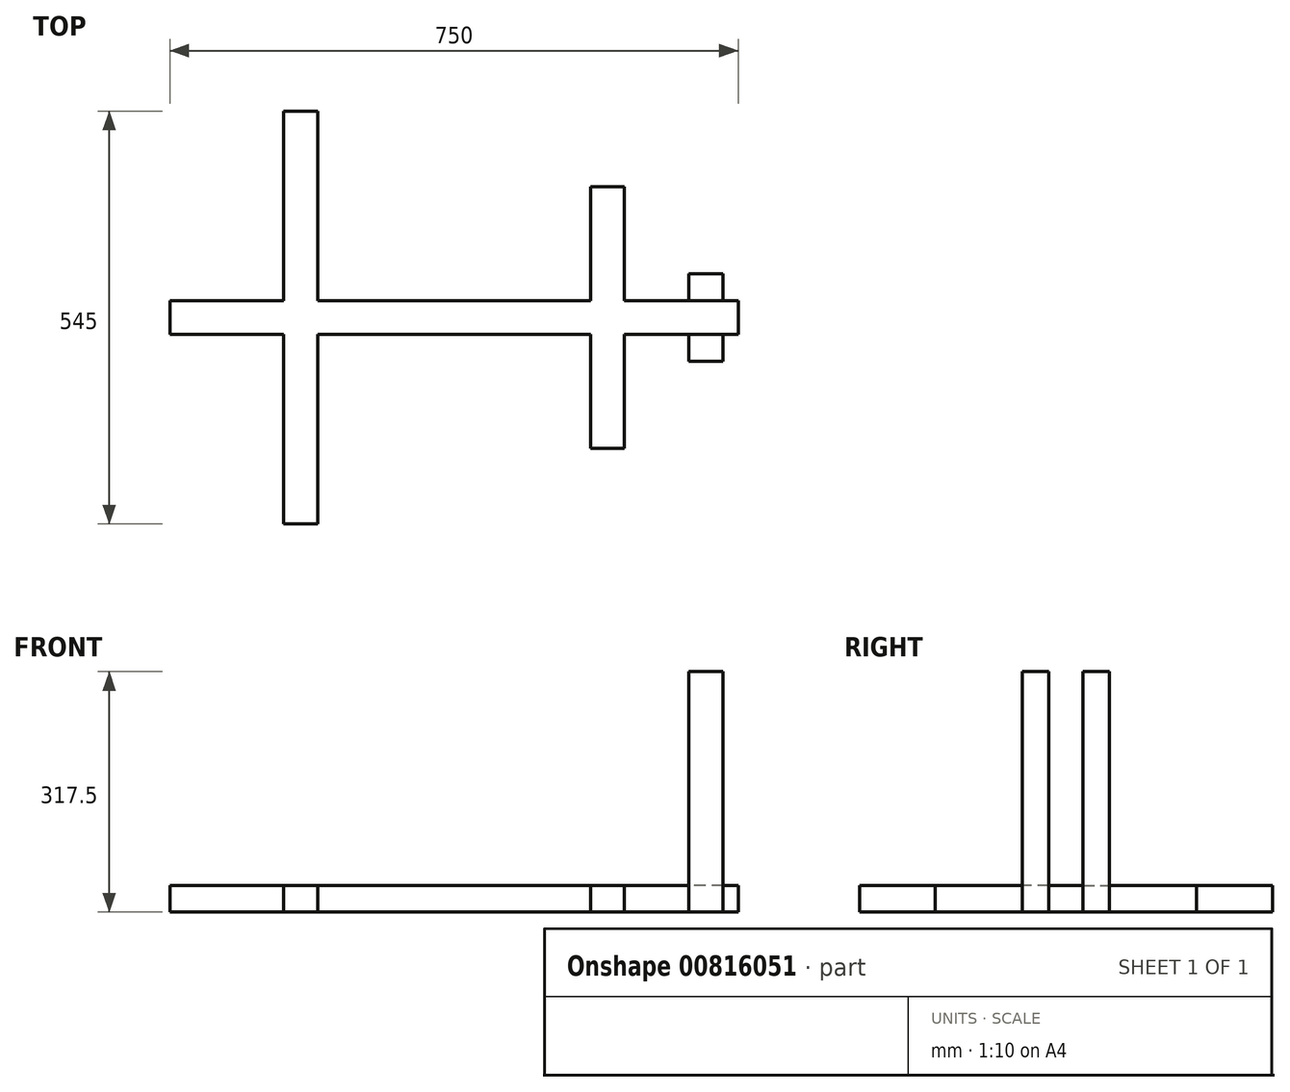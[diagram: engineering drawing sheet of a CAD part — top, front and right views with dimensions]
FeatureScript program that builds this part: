
annotation { "Feature Type Name" : "Feature", "Feature Type Description" : "" }
export const myFeature = defineFeature(function(context is Context, id is Id, definition is map)
    precondition{}
    {
        {
            var Q0;
            Q0=qCreatedBy(makeId("Front.planeOp"),FACE);
            var sketch = newSketch(context, id + "F0", { "sketchPlane" : qUnion([Q0])});
            skLineSegment(sketch, "E0.bottom", {"start": v(375, 17.5) * mm, "end": v(-375, 17.5) * mm});
            skLineSegment(sketch, "E0.top", {"start": v(375, -17.5) * mm, "end": v(-375, -17.5) * mm});
            skLineSegment(sketch, "E0.left", {"start": v(375, 17.5) * mm, "end": v(375, -17.5) * mm});
            skLineSegment(sketch, "E0.right", {"start": v(-375, 17.5) * mm, "end": v(-375, -17.5) * mm});
            skPoint(sketch, "E0.middle", {"position": v(0, 0) * mm});
            skSolve(sketch);
        }
        {
            var Q0;
            Q0=makeQuery(id+"F0.imprint","IMPRINT",FACE,{"disambiguationData":[TD([[makeQuery(id+"F0.imprint","IMPRINT",EDGE,{"derivedFrom":sQuery(id+"F0.wireOp",EDGE,"E0.bottom")}),1.0]])]});
            extrude(context, id + "F1", {"entities" : qUnion([Q0]), "endBound" : BoundingType.SYMMETRIC, "depth" : 45 * mm, "offsetDistance" : 25 * mm, "hasSecondDirection" : true, "secondDirectionOppositeDirection" : true, "secondDirectionDepth" : 25 * mm});
        }
        {
            var Q0;
            Q0=qCreatedBy(makeId("Top.planeOp"),FACE);
            var sketch = newSketch(context, id + "F2", { "sketchPlane" : qUnion([Q0])});
            skLineSegment(sketch, "E1.bottom", {"start": v(-180, 22.5) * mm, "end": v(-225, 22.5) * mm});
            skLineSegment(sketch, "E1.top", {"start": v(-180, 272.5) * mm, "end": v(-225, 272.5) * mm});
            skLineSegment(sketch, "E1.left", {"start": v(-180, 22.5) * mm, "end": v(-180, 272.5) * mm});
            skLineSegment(sketch, "E1.right", {"start": v(-225, 22.5) * mm, "end": v(-225, 272.5) * mm});
            skLineSegment(sketch, "E2", {"start": v(-277.97, 0) * mm, "end": v(292.1, 0) * mm, "construction": true});
            skLineSegment(sketch, "E3.MirrorCS", {"start": v(-225, -22.5) * mm, "end": v(-225, -272.5) * mm});
            skLineSegment(sketch, "E4.MirrorCS", {"start": v(-180, -22.5) * mm, "end": v(-180, -272.5) * mm});
            skLineSegment(sketch, "E5.MirrorCS", {"start": v(-180, -272.5) * mm, "end": v(-225, -272.5) * mm});
            skLineSegment(sketch, "E6.MirrorCS", {"start": v(-180, -22.5) * mm, "end": v(-225, -22.5) * mm});
            skLineSegment(sketch, "E7.bottom", {"start": v(180, 22.5) * mm, "end": v(225, 22.5) * mm});
            skLineSegment(sketch, "E7.top", {"start": v(180, 172.5) * mm, "end": v(225, 172.5) * mm});
            skLineSegment(sketch, "E7.left", {"start": v(180, 22.5) * mm, "end": v(180, 172.5) * mm});
            skLineSegment(sketch, "E7.right", {"start": v(225, 22.5) * mm, "end": v(225, 172.5) * mm});
            skLineSegment(sketch, "E8.MirrorCS", {"start": v(225, -22.5) * mm, "end": v(225, -172.5) * mm});
            skLineSegment(sketch, "E9.MirrorCS", {"start": v(180, -172.5) * mm, "end": v(225, -172.5) * mm});
            skLineSegment(sketch, "E10.MirrorCS", {"start": v(180, -22.5) * mm, "end": v(180, -172.5) * mm});
            skLineSegment(sketch, "E11.MirrorCS", {"start": v(180, -22.5) * mm, "end": v(225, -22.5) * mm});
            skSolve(sketch);
        }
        {
            var Q0;
            Q0=makeQuery(id+"F2.imprint","IMPRINT",FACE,{"disambiguationData":[TD([[makeQuery(id+"F2.imprint","IMPRINT",EDGE,{"derivedFrom":sQuery(id+"F2.wireOp",EDGE,"E7.bottom")}),1.0]])]});
            var Q1;
            Q1=makeQuery(id+"F2.imprint","IMPRINT",FACE,{"disambiguationData":[TD([[makeQuery(id+"F2.imprint","IMPRINT",EDGE,{"derivedFrom":sQuery(id+"F2.wireOp",EDGE,"E8.MirrorCS")}),-1.0]])]});
            var Q2;
            Q2=makeQuery(id+"F2.imprint","IMPRINT",FACE,{"disambiguationData":[TD([[makeQuery(id+"F2.imprint","IMPRINT",EDGE,{"derivedFrom":sQuery(id+"F2.wireOp",EDGE,"E1.bottom")}),-1.0]])]});
            var Q3;
            Q3=makeQuery(id+"F2.imprint","IMPRINT",FACE,{"disambiguationData":[TD([[makeQuery(id+"F2.imprint","IMPRINT",EDGE,{"derivedFrom":sQuery(id+"F2.wireOp",EDGE,"E3.MirrorCS")}),1.0]])]});
            extrude(context, id + "F3", {"entities" : qUnion([Q0, Q1, Q2, Q3]), "operationType" : NewBodyOperationType.ADD, "endBound" : BoundingType.SYMMETRIC, "depth" : 35 * mm, "offsetDistance" : 25 * mm});
        }
        {
            var Q0;
            Q0=qCreatedBy(makeId("Top.planeOp"),FACE);
            var sketch = newSketch(context, id + "F4", { "sketchPlane" : qUnion([Q0])});
            skLineSegment(sketch, "E12.bottom", {"start": v(310, 22.5) * mm, "end": v(355, 22.5) * mm});
            skLineSegment(sketch, "E12.top", {"start": v(310, 57.5) * mm, "end": v(355, 57.5) * mm});
            skLineSegment(sketch, "E12.left", {"start": v(310, 22.5) * mm, "end": v(310, 57.5) * mm});
            skLineSegment(sketch, "E12.right", {"start": v(355, 22.5) * mm, "end": v(355, 57.5) * mm});
            skLineSegment(sketch, "E13", {"start": v(416.08, 0) * mm, "end": v(-404.27, 0) * mm, "construction": true});
            skLineSegment(sketch, "E14.MirrorCS", {"start": v(310, -57.5) * mm, "end": v(355, -57.5) * mm});
            skLineSegment(sketch, "E15.MirrorCS", {"start": v(355, -22.5) * mm, "end": v(355, -57.5) * mm});
            skLineSegment(sketch, "E16.MirrorCS", {"start": v(310, -22.5) * mm, "end": v(355, -22.5) * mm});
            skLineSegment(sketch, "E17.MirrorCS", {"start": v(310, -22.5) * mm, "end": v(310, -57.5) * mm});
            skSolve(sketch);
        }
        {
            var Q0;
            Q0 = qSketchRegion(id + "F4", true);
            extrude(context, id + "F5", {"entities" : qUnion([Q0]), "operationType" : NewBodyOperationType.ADD, "depth" : 300 * mm, "offsetDistance" : 25 * mm, "hasSecondDirection" : true, "secondDirectionOppositeDirection" : true, "secondDirectionDepth" : 17.5 * mm});
        }
    });
